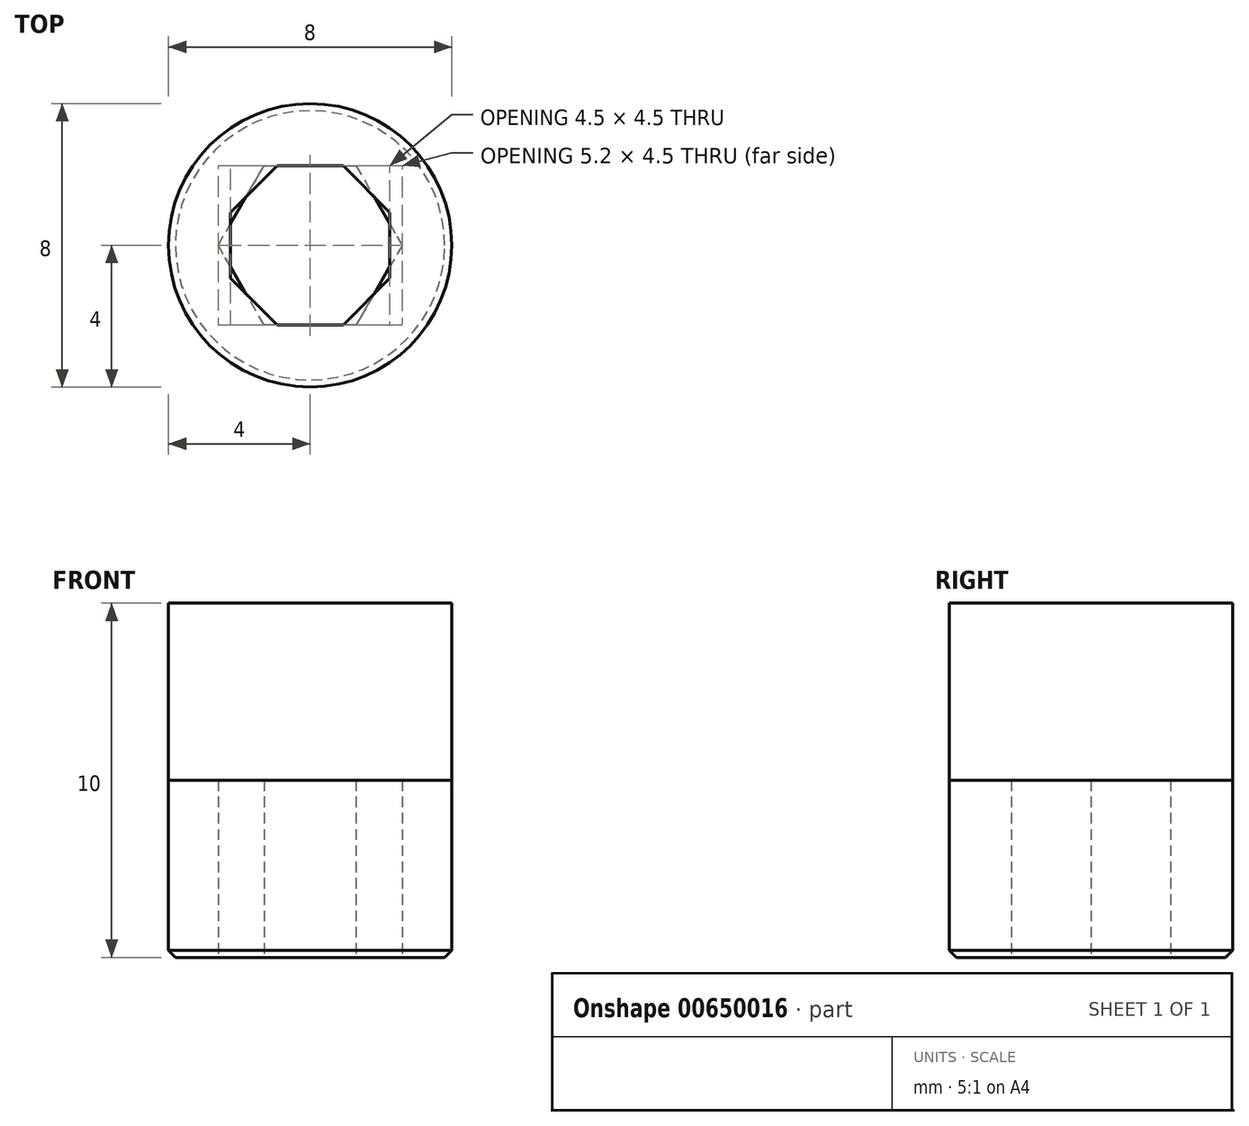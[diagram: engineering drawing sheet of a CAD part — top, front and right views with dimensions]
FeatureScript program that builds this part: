
annotation { "Feature Type Name" : "Feature", "Feature Type Description" : "" }
export const myFeature = defineFeature(function(context is Context, id is Id, definition is map)
    precondition{}
    {
        {
            var Q0;
            Q0=qCreatedBy(makeId("Top.planeOp"),FACE);
            var sketch = newSketch(context, id + "F0", { "sketchPlane" : qUnion([Q0])});
            skCircle(sketch, "E0.cCircle", {"center": v(0, 0) * mm, "radius": 2.25 * mm, "construction": true});
            skLineSegment(sketch, "E0.0", {"start": v(1.3, -2.25) * mm, "end": v(-1.3, -2.25) * mm});
            skLineSegment(sketch, "E0.1", {"start": v(-1.3, -2.25) * mm, "end": v(-2.6, 0) * mm});
            skLineSegment(sketch, "E0.2", {"start": v(-2.6, 0) * mm, "end": v(-1.3, 2.25) * mm});
            skLineSegment(sketch, "E0.3", {"start": v(-1.3, 2.25) * mm, "end": v(1.3, 2.25) * mm});
            skLineSegment(sketch, "E0.4", {"start": v(1.3, 2.25) * mm, "end": v(2.6, 0) * mm});
            skLineSegment(sketch, "E0.5", {"start": v(2.6, 0) * mm, "end": v(1.3, -2.25) * mm});
            skPoint(sketch, "E0.0.midPoint", {"position": v(0, -2.25) * mm});
            skCircle(sketch, "E1", {"center": v(0, 0) * mm, "radius": 4 * mm});
            skSolve(sketch);
        }
        {
            var Q0;
            Q0=makeQuery(id+"F0.imprint","IMPRINT",FACE,{"disambiguationData":[TD([[makeQuery(id+"F0.imprint","IMPRINT",EDGE,{"derivedFrom":sQuery(id+"F0.wireOp",EDGE,"E0.0")}),1.0]])]});
            extrude(context, id + "F1", {"entities" : qUnion([Q0]), "depth" : 5 * mm, "offsetDistance" : 25 * mm});
        }
        {
            var Q0;
            Q0=qCreatedBy(makeId("Top.planeOp"),FACE);
            var sketch = newSketch(context, id + "F2", { "sketchPlane" : qUnion([Q0])});
            skCircle(sketch, "E2.cCircle", {"center": v(0, 0) * mm, "radius": 2.25 * mm, "construction": true});
            skLineSegment(sketch, "E2.0", {"start": v(0.93, -2.25) * mm, "end": v(-0.93, -2.25) * mm});
            skLineSegment(sketch, "E2.1", {"start": v(-0.93, -2.25) * mm, "end": v(-2.25, -0.93) * mm});
            skLineSegment(sketch, "E2.2", {"start": v(-2.25, -0.93) * mm, "end": v(-2.25, 0.93) * mm});
            skLineSegment(sketch, "E2.3", {"start": v(-2.25, 0.93) * mm, "end": v(-0.93, 2.25) * mm});
            skLineSegment(sketch, "E2.4", {"start": v(-0.93, 2.25) * mm, "end": v(0.93, 2.25) * mm});
            skLineSegment(sketch, "E2.5", {"start": v(0.93, 2.25) * mm, "end": v(2.25, 0.93) * mm});
            skLineSegment(sketch, "E2.6", {"start": v(2.25, 0.93) * mm, "end": v(2.25, -0.93) * mm});
            skLineSegment(sketch, "E2.7", {"start": v(2.25, -0.93) * mm, "end": v(0.93, -2.25) * mm});
            skPoint(sketch, "E2.0.midPoint", {"position": v(0, -2.25) * mm});
            skCircle(sketch, "E3", {"center": v(0, 0) * mm, "radius": 4 * mm});
            skSolve(sketch);
        }
        {
            var Q0;
            Q0=makeQuery(id+"F2.imprint","IMPRINT",FACE,{"disambiguationData":[TD([[makeQuery(id+"F2.imprint","IMPRINT",EDGE,{"derivedFrom":sQuery(id+"F2.wireOp",EDGE,"E2.0")}),1.0]])]});
            extrude(context, id + "F3", {"entities" : qUnion([Q0]), "depth" : 10 * mm, "offsetDistance" : 25 * mm});
        }
        {
            var Q0;
            Q0=makeQuery(id+"F3.opExtrude","CAP_EDGE",EDGE,{"disambiguationData":[OSD([sQuery(id+"F2.wireOp",EDGE,"E3")])],"isStart":true});
            chamfer(context, id + "F4", {"entities" : qUnion([Q0]), "width" : .2 * mm, "tangentPropagation" : true});
        }
        {
            var Q0;
            Q0=makeQuery(id+"F1.opExtrude","CAP_EDGE",EDGE,{"disambiguationData":[OSD([sQuery(id+"F0.wireOp",EDGE,"E1")])],"isStart":true});
            chamfer(context, id + "F5", {"entities" : qUnion([Q0]), "width" : .2 * mm, "tangentPropagation" : true});
        }
    });
